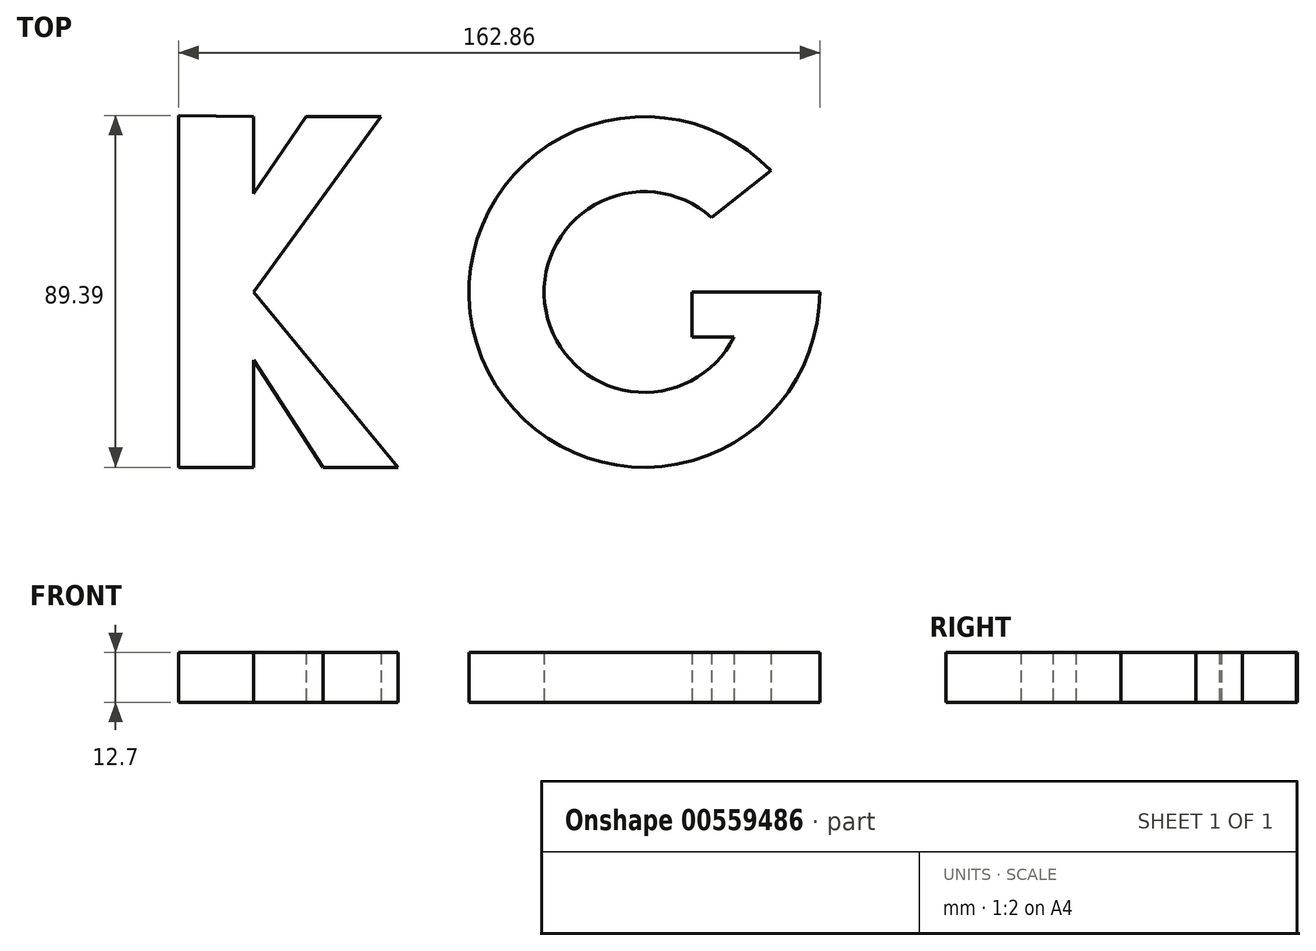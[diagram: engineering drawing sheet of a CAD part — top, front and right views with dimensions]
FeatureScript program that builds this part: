
annotation { "Feature Type Name" : "Feature", "Feature Type Description" : "" }
export const myFeature = defineFeature(function(context is Context, id is Id, definition is map)
    precondition{}
    {
        {
            var Q0;
            Q0=qCreatedBy(makeId("Top.planeOp"),FACE);
            var sketch = newSketch(context, id + "F0", { "sketchPlane" : qUnion([Q0])});
            skLineSegment(sketch, "E0", {"start": v(-55.75, 44.84) * mm, "end": v(-55.75, -44.55) * mm});
            skLineSegment(sketch, "E1", {"start": v(-55.75, -44.55) * mm, "end": v(-36.7, -44.55) * mm});
            skLineSegment(sketch, "E2", {"start": v(-36.7, -44.55) * mm, "end": v(-36.7, -17.33) * mm});
            skLineSegment(sketch, "E3", {"start": v(-36.7, -17.33) * mm, "end": v(-19.05, -44.55) * mm});
            skLineSegment(sketch, "E4", {"start": v(-19.05, -44.55) * mm, "end": v(0, -44.55) * mm});
            skLineSegment(sketch, "E5", {"start": v(0, -44.55) * mm, "end": v(-36.7, 0) * mm});
            skLineSegment(sketch, "E6", {"start": v(-36.7, 0) * mm, "end": v(-4.4, 44.55) * mm});
            skLineSegment(sketch, "E7", {"start": v(-4.4, 44.55) * mm, "end": v(-23.45, 44.55) * mm});
            skLineSegment(sketch, "E8", {"start": v(-23.45, 44.55) * mm, "end": v(-36.7, 24.96) * mm});
            skLineSegment(sketch, "E9", {"start": v(-36.7, 24.96) * mm, "end": v(-36.7, 44.55) * mm});
            skLineSegment(sketch, "E10", {"start": v(-36.7, 44.55) * mm, "end": v(-55.75, 44.84) * mm});
            skArc(sketch, "E11", {"start": v(94.7, 30.84) * mm, "mid": v(21.23, -16.62) * mm, "end": v(107.11, 0) * mm});
            skLineSegment(sketch, "E12", {"start": v(62.56, 44.55) * mm, "end": v(65.87, 44.55) * mm});
            skLineSegment(sketch, "E13", {"start": v(62.56, -44.55) * mm, "end": v(65.87, -44.55) * mm});
            skArc(sketch, "E14", {"start": v(79.58, 18.99) * mm, "mid": v(37.51, -4.75) * mm, "end": v(85.36, -11.43) * mm});
            skLineSegment(sketch, "E15", {"start": v(79.58, 18.99) * mm, "end": v(94.7, 30.84) * mm});
            skLineSegment(sketch, "E16", {"start": v(88.06, 0) * mm, "end": v(107.11, 0) * mm});
            skLineSegment(sketch, "E17", {"start": v(88.06, 0) * mm, "end": v(74.71, 0) * mm});
            skLineSegment(sketch, "E18", {"start": v(74.71, 0) * mm, "end": v(74.71, -11.43) * mm});
            skLineSegment(sketch, "E19", {"start": v(74.71, -11.43) * mm, "end": v(85.36, -11.43) * mm});
            skSolve(sketch);
        }
        {
            var Q0;
            Q0 = qSketchRegion(id + "F0", true);
            extrude(context, id + "F1", {"entities" : qUnion([Q0]), "depth" : 12.7 * mm, "offsetDistance" : 25.4 * mm});
        }
    });
